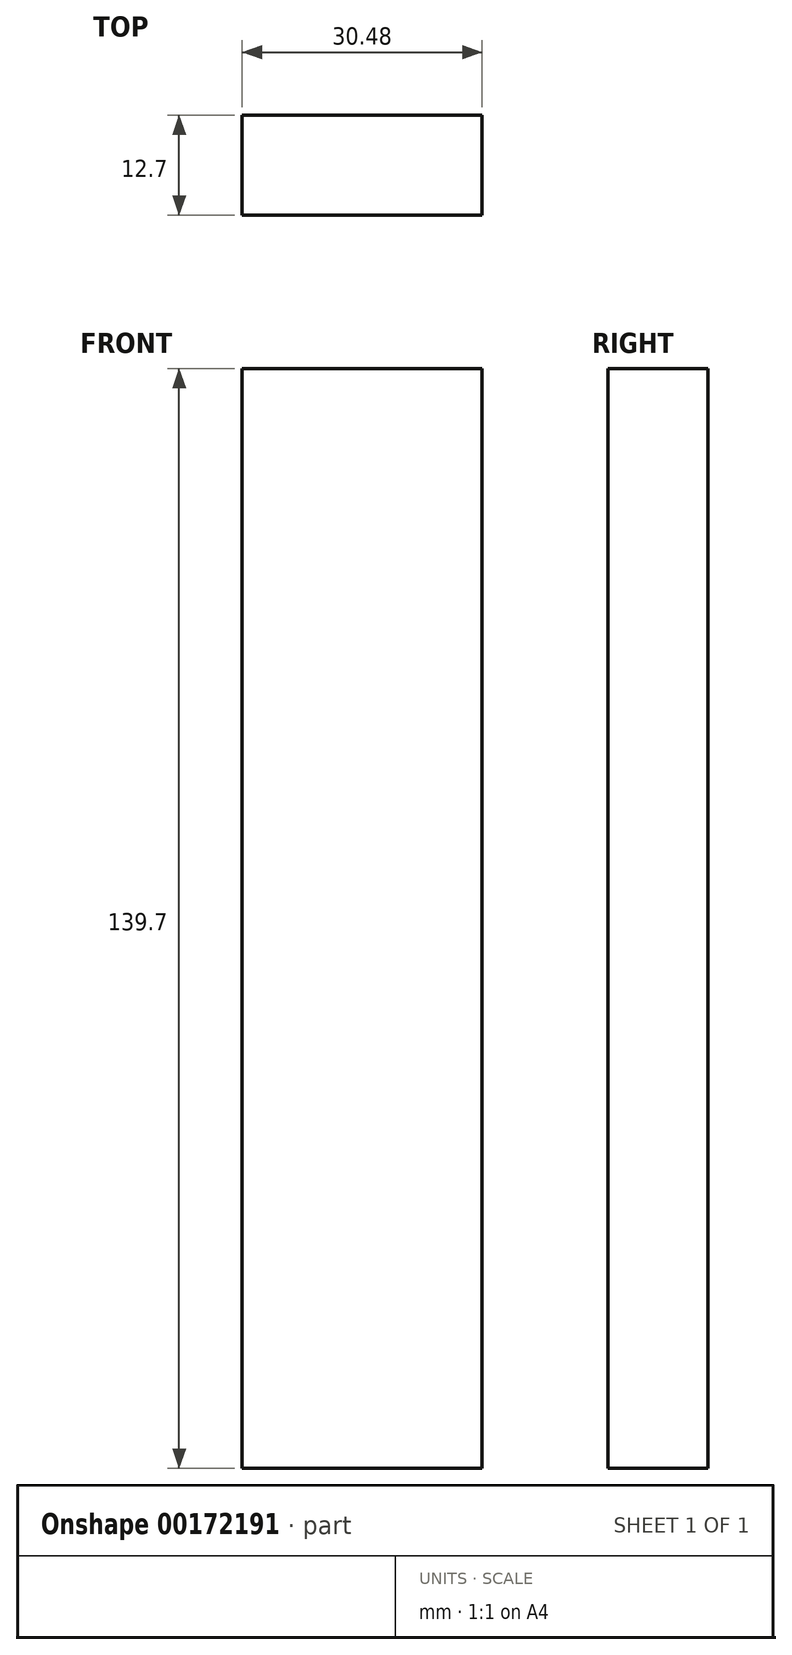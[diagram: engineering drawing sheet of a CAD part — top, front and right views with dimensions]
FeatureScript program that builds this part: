
annotation { "Feature Type Name" : "Feature", "Feature Type Description" : "" }
export const myFeature = defineFeature(function(context is Context, id is Id, definition is map)
    precondition{}
    {
        {
            var Q0;
            Q0=qCreatedBy(makeId("Front.planeOp"),FACE);
            var sketch = newSketch(context, id + "F0", { "sketchPlane" : qUnion([Q0])});
            skLineSegment(sketch, "E0.bottom", {"start": v(-54.66, 60.17) * mm, "end": v(-24.18, 60.17) * mm});
            skLineSegment(sketch, "E0.top", {"start": v(-54.66, -79.53) * mm, "end": v(-24.18, -79.53) * mm});
            skLineSegment(sketch, "E0.left", {"start": v(-54.66, 60.17) * mm, "end": v(-54.66, -79.53) * mm});
            skLineSegment(sketch, "E0.right", {"start": v(-24.18, 60.17) * mm, "end": v(-24.18, -79.53) * mm});
            skSolve(sketch);
        }
        {
            var Q0;
            Q0 = qSketchRegion(id + "F0", true);
            extrude(context, id + "F1", {"entities" : qUnion([Q0]), "depth" : 12.7 * mm});
        }
    });
